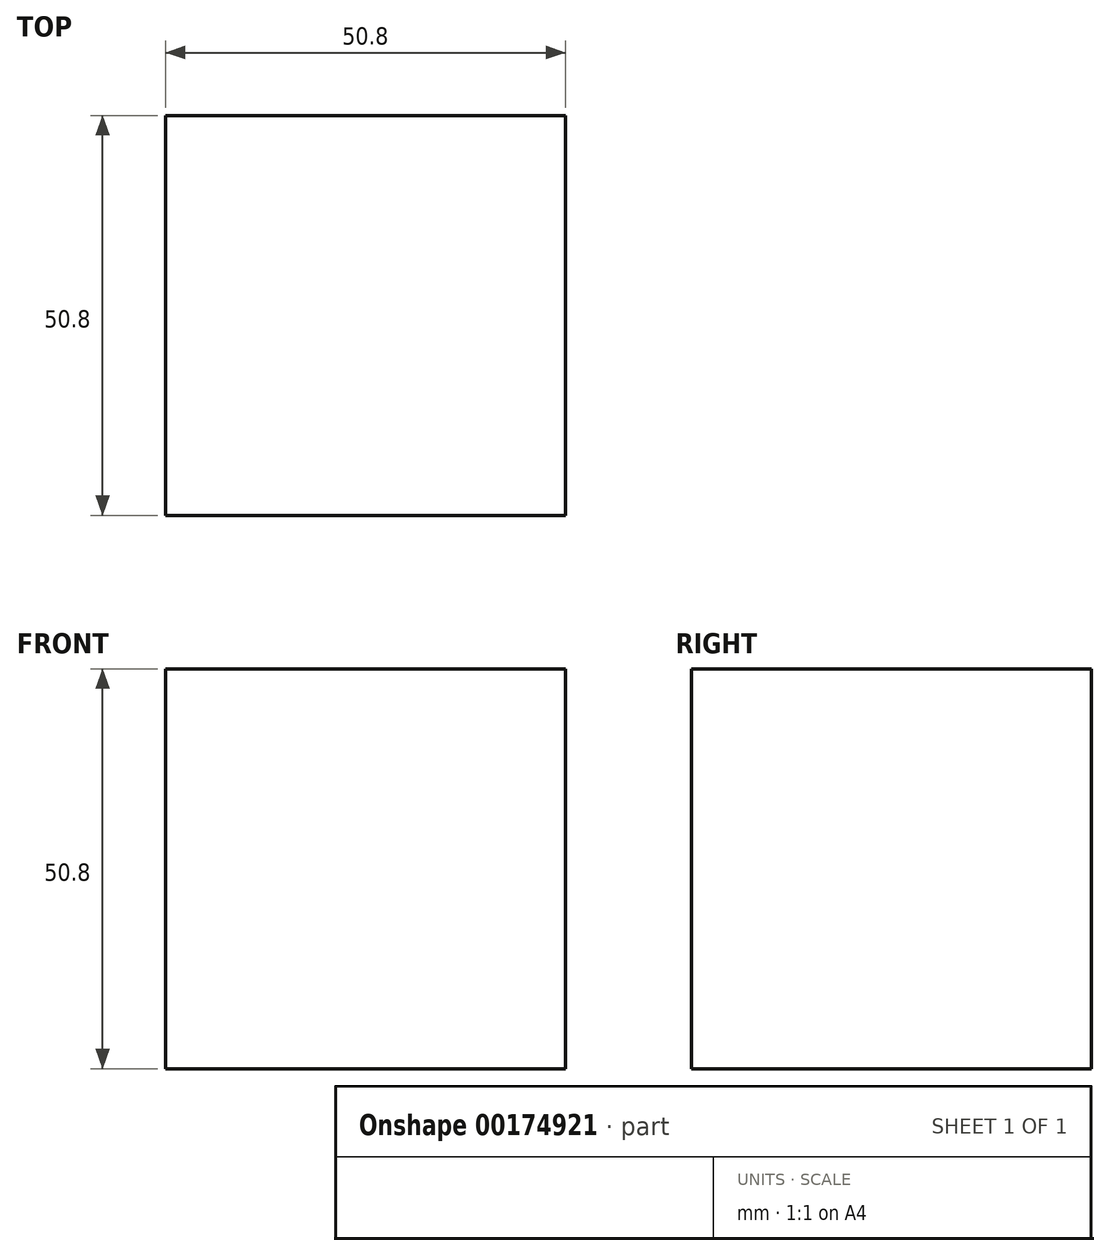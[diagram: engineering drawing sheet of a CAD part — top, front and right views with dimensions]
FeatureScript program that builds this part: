
annotation { "Feature Type Name" : "Feature", "Feature Type Description" : "" }
export const myFeature = defineFeature(function(context is Context, id is Id, definition is map)
    precondition{}
    {
        {
            var Q0;
            Q0=qCreatedBy(makeId("Front.planeOp"),FACE);
            var sketch = newSketch(context, id + "F0", { "sketchPlane" : qUnion([Q0])});
            skLineSegment(sketch, "E0.bottom", {"start": v(0, 0) * mm, "end": v(50.8, 0) * mm});
            skLineSegment(sketch, "E0.top", {"start": v(0, 50.8) * mm, "end": v(50.8, 50.8) * mm});
            skLineSegment(sketch, "E0.left", {"start": v(0, 0) * mm, "end": v(0, 50.8) * mm});
            skLineSegment(sketch, "E0.right", {"start": v(50.8, 0) * mm, "end": v(50.8, 50.8) * mm});
            skSolve(sketch);
        }
        {
            var Q0;
            Q0=makeQuery(id+"F0.imprint","IMPRINT",FACE,{"disambiguationData":[TD([[makeQuery(id+"F0.imprint","IMPRINT",EDGE,{"derivedFrom":sQuery(id+"F0.wireOp",EDGE,"E0.bottom")}),1.0]])]});
            extrude(context, id + "F1", {"entities" : qUnion([Q0]), "depth" : 50.8 * mm});
        }
    });
